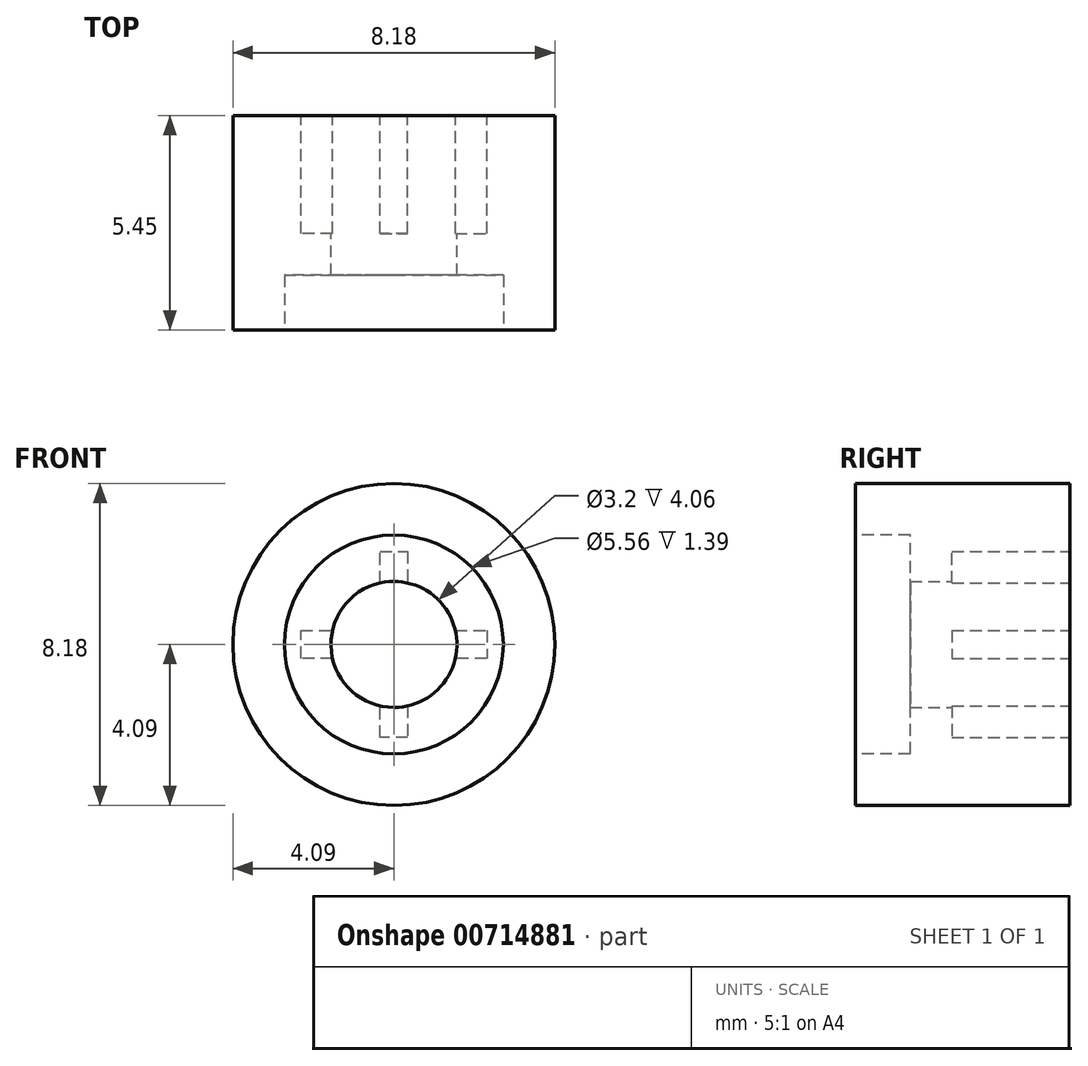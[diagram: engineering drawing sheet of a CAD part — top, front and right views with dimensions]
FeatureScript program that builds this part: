
annotation { "Feature Type Name" : "Feature", "Feature Type Description" : "" }
export const myFeature = defineFeature(function(context is Context, id is Id, definition is map)
    precondition{}
    {
        {
            var Q0;
            Q0=qCreatedBy(makeId("Front.planeOp"),FACE);
            var sketch = newSketch(context, id + "F0", { "sketchPlane" : qUnion([Q0])});
            skCircle(sketch, "E0", {"center": v(0, 0) * mm, "radius": 1.6 * mm});
            skCircle(sketch, "E1", {"center": v(0, 0) * mm, "radius": 4.1 * mm});
            skSolve(sketch);
        }
        {
            var Q0;
            Q0 = qSketchRegion(id + "F0", true);
            extrude(context, id + "F1", {"entities" : qUnion([Q0]), "depth" : 5.45 * mm, "offsetDistance" : 25 * mm});
        }
        {
            var Q0;
            Q0=makeQuery(id+"F1.opExtrude","CAP_FACE",FACE,{"disambiguationData":[OSD([sQuery(id+"F0.wireOp",EDGE,"E0"),sQuery(id+"F0.wireOp",EDGE,"E1")])],"isStart":false});
            var sketch = newSketch(context, id + "F2", { "sketchPlane" : qUnion([Q0])});
            skCircle(sketch, "E2", {"center": v(0, 0) * mm, "radius": 2.78 * mm});
            skSolve(sketch);
        }
        {
            var Q0;
            Q0 = qSketchRegion(id + "F2", true);
            extrude(context, id + "F3", {"entities" : qUnion([Q0]), "operationType" : NewBodyOperationType.REMOVE, "oppositeDirection" : true, "depth" : 1.39 * mm, "offsetDistance" : 25 * mm});
        }
        {
            var Q0;
            Q0=makeQuery(id+"F1.opExtrude","CAP_FACE",FACE,{"disambiguationData":[OSD([sQuery(id+"F0.wireOp",EDGE,"E0"),sQuery(id+"F0.wireOp",EDGE,"E1")])],"isStart":true});
            var sketch = newSketch(context, id + "F4", { "sketchPlane" : qUnion([Q0])});
            skLineSegment(sketch, "E3", {"start": v(-1.56, 0.35) * mm, "end": v(-2.36, 0.35) * mm});
            skLineSegment(sketch, "E4", {"start": v(-2.36, 0.35) * mm, "end": v(-2.36, -0.35) * mm});
            skLineSegment(sketch, "E5", {"start": v(-2.36, -0.35) * mm, "end": v(-1.56, -0.35) * mm});
            skPoint(sketch, "E6", {"position": v(-2.36, 0) * mm});
            skLineSegment(sketch, "E7.1.0", {"start": v(-0.35, -1.56) * mm, "end": v(-0.35, -2.36) * mm});
            skLineSegment(sketch, "E7.1.1", {"start": v(0.35, -2.36) * mm, "end": v(0.35, -1.56) * mm});
            skLineSegment(sketch, "E7.1.2", {"start": v(-0.35, -2.36) * mm, "end": v(0.35, -2.36) * mm});
            skLineSegment(sketch, "E7.2.0", {"start": v(1.56, -0.35) * mm, "end": v(2.36, -0.35) * mm});
            skLineSegment(sketch, "E7.2.1", {"start": v(2.36, 0.35) * mm, "end": v(1.56, 0.35) * mm});
            skLineSegment(sketch, "E7.2.2", {"start": v(2.36, -0.35) * mm, "end": v(2.36, 0.35) * mm});
            skLineSegment(sketch, "E7.3.0", {"start": v(0.35, 1.56) * mm, "end": v(0.35, 2.36) * mm});
            skLineSegment(sketch, "E7.3.1", {"start": v(-0.35, 2.36) * mm, "end": v(-0.35, 1.56) * mm});
            skLineSegment(sketch, "E7.3.2", {"start": v(0.35, 2.36) * mm, "end": v(-0.35, 2.36) * mm});
            skPoint(sketch, "E7.center", {"position": v(0, 0) * mm});
            skSolve(sketch);
        }
        {
            var Q0;
            {var subQ0=sQuery(id+"F4.wireOp",EDGE,"E7.3.0");Q0=makeQuery(id+"F4.imprint","IMPRINT",FACE,{"disambiguationData":[TD([[makeQuery(id+"F4.imprint","IMPRINT",EDGE,{"derivedFrom":subQ0}),1.0]])]});}
            var Q1;
            {var subQ0=sQuery(id+"F4.wireOp",EDGE,"E7.2.0");Q1=makeQuery(id+"F4.imprint","IMPRINT",FACE,{"disambiguationData":[TD([[makeQuery(id+"F4.imprint","IMPRINT",EDGE,{"derivedFrom":subQ0}),1.0]])]});}
            var Q2;
            {var subQ0=sQuery(id+"F4.wireOp",EDGE,"E7.1.0");Q2=makeQuery(id+"F4.imprint","IMPRINT",FACE,{"disambiguationData":[TD([[makeQuery(id+"F4.imprint","IMPRINT",EDGE,{"derivedFrom":subQ0}),1.0]])]});}
            var Q3;
            {var subQ0=sQuery(id+"F4.wireOp",EDGE,"E3");Q3=makeQuery(id+"F4.imprint","IMPRINT",FACE,{"disambiguationData":[TD([[makeQuery(id+"F4.imprint","IMPRINT",EDGE,{"derivedFrom":subQ0}),1.0]])]});}
            extrude(context, id + "F5", {"entities" : qUnion([Q0, Q1, Q2, Q3]), "operationType" : NewBodyOperationType.REMOVE, "oppositeDirection" : true, "depth" : 3 * mm, "offsetDistance" : 25 * mm});
        }
    });
